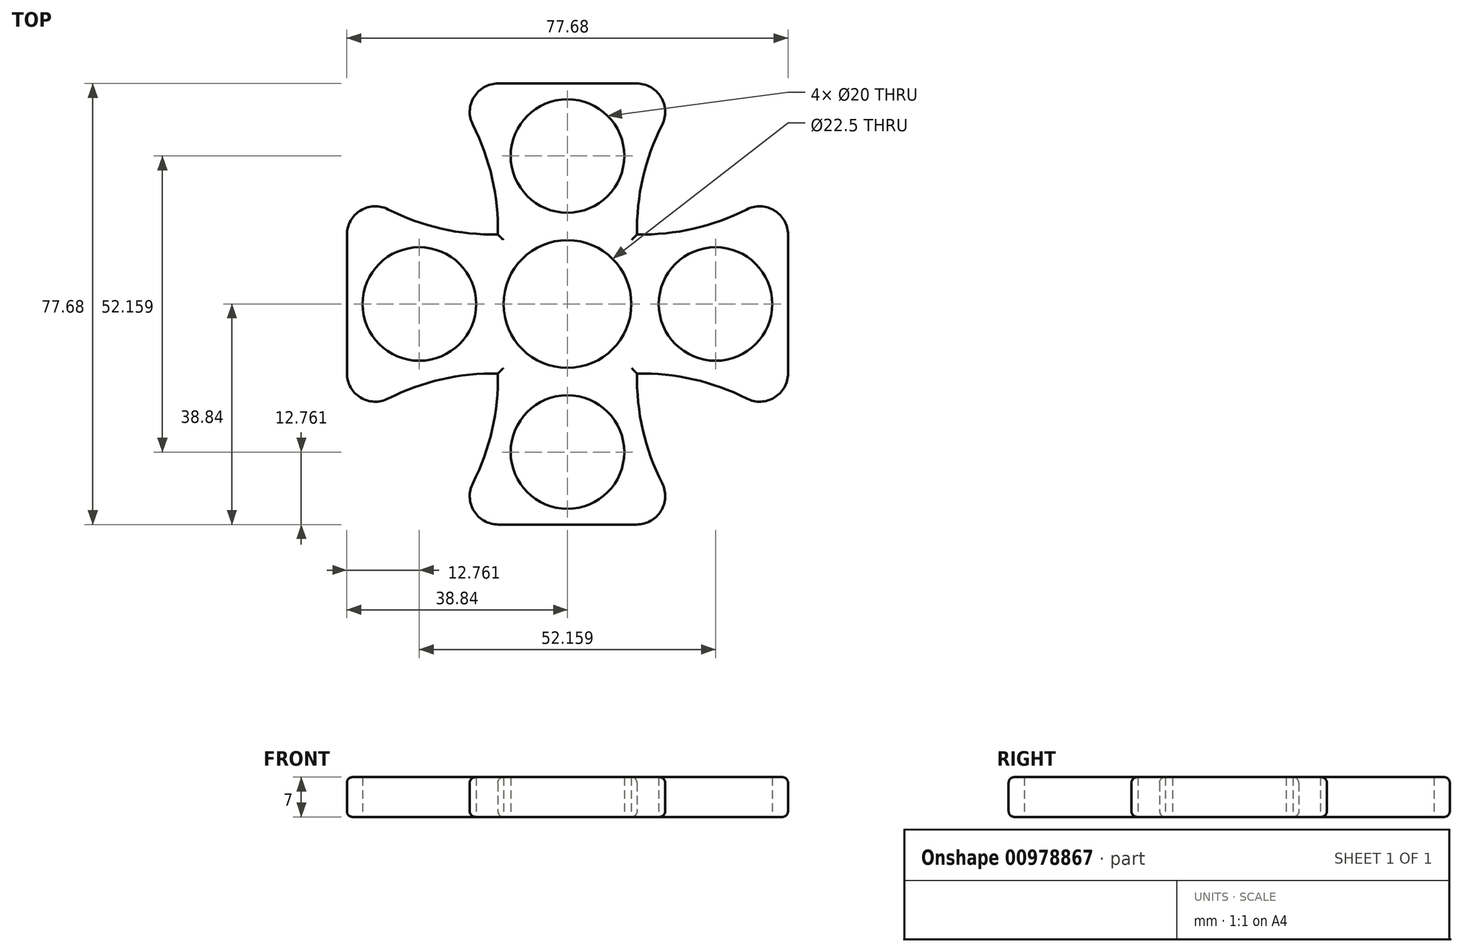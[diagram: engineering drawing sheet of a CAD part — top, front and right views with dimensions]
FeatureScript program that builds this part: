
annotation { "Feature Type Name" : "Feature", "Feature Type Description" : "" }
export const myFeature = defineFeature(function(context is Context, id is Id, definition is map)
    precondition{}
    {
        {
            var Q0;
            Q0=qCreatedBy(makeId("Top.planeOp"),FACE);
            var sketch = newSketch(context, id + "F0", { "sketchPlane" : qUnion([Q0])});
            skPoint(sketch, "E0.center", {"position": v(0, 0) * mm});
            skCircle(sketch, "E1", {"center": v(0, 26.08) * mm, "radius": 10 * mm});
            skArc(sketch, "E2.MirrorCS", {"start": v(-12.25, 12.25) * mm, "mid": v(-26.36, 14.45) * mm, "end": v(-38.84, 21.4) * mm});
            skCircle(sketch, "E3.MirrorC", {"center": v(-26.08, 0) * mm, "radius": 10 * mm});
            skCircle(sketch, "E4.MirrorC", {"center": v(26.08, 0) * mm, "radius": 10 * mm});
            skCircle(sketch, "E5.MirrorC", {"center": v(0, -26.08) * mm, "radius": 10 * mm});
            skLineSegment(sketch, "E6", {"start": v(0, 3.97) * mm, "end": v(0, -3.51) * mm});
            skLineSegment(sketch, "E7", {"start": v(-3.24, 0) * mm, "end": v(3.55, 0) * mm});
            skLineSegment(sketch, "E8", {"start": v(24.25, 0) * mm, "end": v(28.78, 0) * mm});
            skLineSegment(sketch, "E9", {"start": v(26.08, 2.92) * mm, "end": v(26.08, -2.47) * mm});
            skLineSegment(sketch, "E10", {"start": v(0, 29.55) * mm, "end": v(0, 21.89) * mm});
            skLineSegment(sketch, "E11", {"start": v(-3.94, 26.08) * mm, "end": v(3.02, 26.08) * mm});
            skLineSegment(sketch, "E12", {"start": v(0, -22.13) * mm, "end": v(0, -30.31) * mm});
            skLineSegment(sketch, "E13", {"start": v(-3.24, -26.08) * mm, "end": v(3.72, -26.08) * mm});
            skLineSegment(sketch, "E14", {"start": v(-26.08, 2.75) * mm, "end": v(-26.08, -3.51) * mm});
            skLineSegment(sketch, "E15", {"start": v(-28.64, 0) * mm, "end": v(-22.73, 0) * mm});
            skCircle(sketch, "E16", {"center": v(0, 0) * mm, "radius": 11.25 * mm});
            skArc(sketch, "E17.MirrorCS", {"start": v(-12.25, -12.25) * mm, "mid": v(-26.36, -14.45) * mm, "end": v(-38.84, -21.4) * mm});
            skLineSegment(sketch, "E18", {"start": v(-38.84, 21.4) * mm, "end": v(-38.84, -21.4) * mm});
            skArc(sketch, "E19.MirrorCS", {"start": v(-12.25, 12.25) * mm, "mid": v(-14.45, 26.36) * mm, "end": v(-21.4, 38.84) * mm});
            skLineSegment(sketch, "E20.MirrorCS", {"start": v(-21.4, 38.84) * mm, "end": v(21.4, 38.84) * mm});
            skArc(sketch, "E21.MirrorCS", {"start": v(12.25, 12.25) * mm, "mid": v(14.45, 26.36) * mm, "end": v(21.4, 38.84) * mm});
            skArc(sketch, "E22.MirrorCS", {"start": v(-12.25, -12.25) * mm, "mid": v(-14.45, -26.36) * mm, "end": v(-21.4, -38.84) * mm});
            skLineSegment(sketch, "E23.MirrorCS", {"start": v(21.4, -38.84) * mm, "end": v(-21.4, -38.84) * mm});
            skArc(sketch, "E24.MirrorCS", {"start": v(12.25, -12.25) * mm, "mid": v(14.45, -26.36) * mm, "end": v(21.4, -38.84) * mm});
            skArc(sketch, "E25.MirrorCS", {"start": v(12.25, 12.25) * mm, "mid": v(26.36, 14.45) * mm, "end": v(38.84, 21.4) * mm});
            skLineSegment(sketch, "E26.MirrorCS", {"start": v(38.84, 21.4) * mm, "end": v(38.84, -21.4) * mm});
            skArc(sketch, "E27.MirrorCS", {"start": v(12.25, -12.25) * mm, "mid": v(26.36, -14.45) * mm, "end": v(38.84, -21.4) * mm});
            skSolve(sketch);
        }
        {
            var Q0;
            Q0=qSketchRegion(id+"F0",true);
            extrude(context, id + "F1", {"entities" : qUnion([Q0]), "depth" : 7 * mm, "offsetDistance" : 25 * mm});
        }
        {
            var Q0;
            Q0=makeQuery(id+"F1.opExtrude","CAP_EDGE",EDGE,{"disambiguationData":[OSD([sQuery(id+"F0.wireOp",EDGE,"E21.MirrorCS")])],"isStart":false});
            var Q1;
            Q1=makeQuery(id+"F1.opExtrude","CAP_EDGE",EDGE,{"disambiguationData":[OSD([sQuery(id+"F0.wireOp",EDGE,"E19.MirrorCS")])],"isStart":false});
            var Q2;
            Q2=makeQuery(id+"F1.opExtrude","CAP_EDGE",EDGE,{"disambiguationData":[OSD([sQuery(id+"F0.wireOp",EDGE,"E2.MirrorCS")])],"isStart":false});
            var Q3;
            Q3=makeQuery(id+"F1.opExtrude","CAP_EDGE",EDGE,{"disambiguationData":[OSD([sQuery(id+"F0.wireOp",EDGE,"E18")])],"isStart":false});
            var Q4;
            Q4=makeQuery(id+"F1.opExtrude","CAP_EDGE",EDGE,{"disambiguationData":[OSD([sQuery(id+"F0.wireOp",EDGE,"E17.MirrorCS")])],"isStart":false});
            var Q5;
            Q5=makeQuery(id+"F1.opExtrude","CAP_EDGE",EDGE,{"disambiguationData":[OSD([sQuery(id+"F0.wireOp",EDGE,"E22.MirrorCS")])],"isStart":false});
            var Q6;
            Q6=makeQuery(id+"F1.opExtrude","CAP_EDGE",EDGE,{"disambiguationData":[OSD([sQuery(id+"F0.wireOp",EDGE,"E23.MirrorCS")])],"isStart":false});
            var Q7;
            Q7=makeQuery(id+"F1.opExtrude","CAP_EDGE",EDGE,{"disambiguationData":[OSD([sQuery(id+"F0.wireOp",EDGE,"E24.MirrorCS")])],"isStart":false});
            var Q8;
            Q8=makeQuery(id+"F1.opExtrude","CAP_EDGE",EDGE,{"disambiguationData":[OSD([sQuery(id+"F0.wireOp",EDGE,"E27.MirrorCS")])],"isStart":false});
            var Q9;
            Q9=makeQuery(id+"F1.opExtrude","CAP_EDGE",EDGE,{"disambiguationData":[OSD([sQuery(id+"F0.wireOp",EDGE,"E26.MirrorCS")])],"isStart":false});
            var Q10;
            Q10=makeQuery(id+"F1.opExtrude","CAP_EDGE",EDGE,{"disambiguationData":[OSD([sQuery(id+"F0.wireOp",EDGE,"E25.MirrorCS")])],"isStart":false});
            var Q11;
            Q11=makeQuery(id+"F1.opExtrude","CAP_EDGE",EDGE,{"disambiguationData":[OSD([sQuery(id+"F0.wireOp",EDGE,"E20.MirrorCS")])],"isStart":false});
            var Q12;
            Q12=makeQuery(id+"F1.opExtrude","CAP_EDGE",EDGE,{"disambiguationData":[OSD([sQuery(id+"F0.wireOp",EDGE,"E20.MirrorCS")])],"isStart":true});
            var Q13;
            Q13=makeQuery(id+"F1.opExtrude","CAP_EDGE",EDGE,{"disambiguationData":[OSD([sQuery(id+"F0.wireOp",EDGE,"E26.MirrorCS")])],"isStart":true});
            var Q14;
            Q14=makeQuery(id+"F1.opExtrude","CAP_EDGE",EDGE,{"disambiguationData":[OSD([sQuery(id+"F0.wireOp",EDGE,"E27.MirrorCS")])],"isStart":true});
            var Q15;
            Q15=makeQuery(id+"F1.opExtrude","CAP_EDGE",EDGE,{"disambiguationData":[OSD([sQuery(id+"F0.wireOp",EDGE,"E23.MirrorCS")])],"isStart":true});
            var Q16;
            Q16=makeQuery(id+"F1.opExtrude","CAP_EDGE",EDGE,{"disambiguationData":[OSD([sQuery(id+"F0.wireOp",EDGE,"E18")])],"isStart":true});
            var Q17;
            Q17=makeQuery(id+"F1.opExtrude","CAP_EDGE",EDGE,{"disambiguationData":[OSD([sQuery(id+"F0.wireOp",EDGE,"E17.MirrorCS")])],"isStart":true});
            var Q18;
            Q18=makeQuery(id+"F1.opExtrude","CAP_EDGE",EDGE,{"disambiguationData":[OSD([sQuery(id+"F0.wireOp",EDGE,"E21.MirrorCS")])],"isStart":true});
            var Q19;
            Q19=makeQuery(id+"F1.opExtrude","CAP_EDGE",EDGE,{"disambiguationData":[OSD([sQuery(id+"F0.wireOp",EDGE,"E25.MirrorCS")])],"isStart":true});
            var Q20;
            Q20=makeQuery(id+"F1.opExtrude","CAP_EDGE",EDGE,{"disambiguationData":[OSD([sQuery(id+"F0.wireOp",EDGE,"E22.MirrorCS")])],"isStart":true});
            var Q21;
            Q21=makeQuery(id+"F1.opExtrude","CAP_EDGE",EDGE,{"disambiguationData":[OSD([sQuery(id+"F0.wireOp",EDGE,"E24.MirrorCS")])],"isStart":true});
            var Q22;
            Q22=makeQuery(id+"F1.opExtrude","CAP_EDGE",EDGE,{"disambiguationData":[OSD([sQuery(id+"F0.wireOp",EDGE,"E19.MirrorCS")])],"isStart":true});
            var Q23;
            Q23=makeQuery(id+"F1.opExtrude","CAP_EDGE",EDGE,{"disambiguationData":[OSD([sQuery(id+"F0.wireOp",EDGE,"E2.MirrorCS")])],"isStart":true});
            fillet(context, id + "F2", {"entities" : qUnion([Q0, Q1, Q2, Q3, Q4, Q5, Q6, Q7, Q8, Q9, Q10, Q11, Q12, Q13, Q14, Q15, Q16, Q17, Q18, Q19, Q20, Q21, Q22, Q23]), "radius" : 1 * mm, "tangentPropagation" : true, "allowEdgeOverflow" : false});
        }
        {
            var Q0;
            Q0=makeQuery(id+"F1.opExtrude","SWEPT_EDGE",EDGE,{"disambiguationData":[OSD([sQuery(id+"F0.wireOp",EDGE,"E26.MirrorCS"),sQuery(id+"F0.wireOp",EDGE,"E27.MirrorCS")])]});
            var Q1;
            Q1=makeQuery(id+"F2.opFillet","BLEND_EDGE",EDGE,{"blendedFrom":[makeQuery(id+"F1.opExtrude","CAP_EDGE",EDGE,{"disambiguationData":[OSD([sQuery(id+"F0.wireOp",EDGE,"E25.MirrorCS")])],"isStart":true}),makeQuery(id+"F1.opExtrude","CAP_EDGE",EDGE,{"disambiguationData":[OSD([sQuery(id+"F0.wireOp",EDGE,"E26.MirrorCS")])],"isStart":true})],"blendedInto":[]});
            var Q2;
            Q2=makeQuery(id+"F1.opExtrude","SWEPT_EDGE",EDGE,{"disambiguationData":[OSD([sQuery(id+"F0.wireOp",EDGE,"E20.MirrorCS"),sQuery(id+"F0.wireOp",EDGE,"E21.MirrorCS")])]});
            var Q3;
            Q3=makeQuery(id+"F1.opExtrude","SWEPT_EDGE",EDGE,{"disambiguationData":[OSD([sQuery(id+"F0.wireOp",EDGE,"E19.MirrorCS"),sQuery(id+"F0.wireOp",EDGE,"E20.MirrorCS")])]});
            var Q4;
            Q4=makeQuery(id+"F1.opExtrude","SWEPT_EDGE",EDGE,{"disambiguationData":[OSD([sQuery(id+"F0.wireOp",EDGE,"E2.MirrorCS"),sQuery(id+"F0.wireOp",EDGE,"E18")])]});
            var Q5;
            Q5=makeQuery(id+"F1.opExtrude","SWEPT_EDGE",EDGE,{"disambiguationData":[OSD([sQuery(id+"F0.wireOp",EDGE,"E17.MirrorCS"),sQuery(id+"F0.wireOp",EDGE,"E18")])]});
            var Q6;
            Q6=makeQuery(id+"F1.opExtrude","SWEPT_EDGE",EDGE,{"disambiguationData":[OSD([sQuery(id+"F0.wireOp",EDGE,"E22.MirrorCS"),sQuery(id+"F0.wireOp",EDGE,"E23.MirrorCS")])]});
            var Q7;
            Q7=makeQuery(id+"F1.opExtrude","SWEPT_EDGE",EDGE,{"disambiguationData":[OSD([sQuery(id+"F0.wireOp",EDGE,"E23.MirrorCS"),sQuery(id+"F0.wireOp",EDGE,"E24.MirrorCS")])]});
            fillet(context, id + "F3", {"entities" : qUnion([Q0, Q1, Q2, Q3, Q4, Q5, Q6, Q7]), "radius" : 5 * mm, "tangentPropagation" : true, "allowEdgeOverflow" : false});
        }
    });
